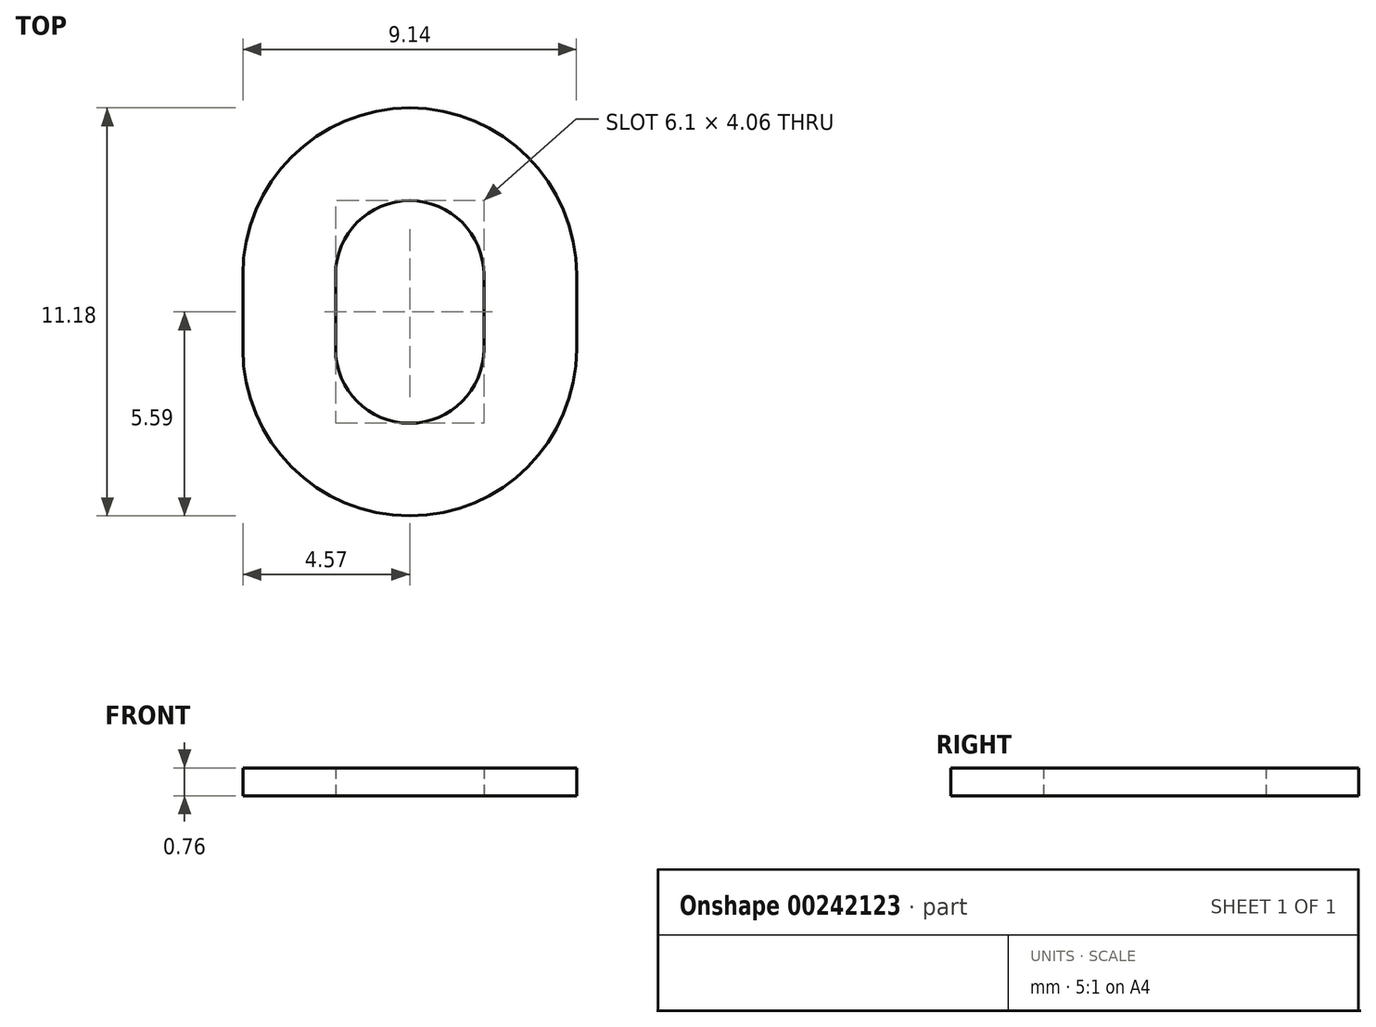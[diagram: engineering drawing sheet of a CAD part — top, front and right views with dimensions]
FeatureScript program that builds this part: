
annotation { "Feature Type Name" : "Feature", "Feature Type Description" : "" }
export const myFeature = defineFeature(function(context is Context, id is Id, definition is map)
    precondition{}
    {
        {
            var Q0;
            Q0=qCreatedBy(makeId("Top.planeOp"),FACE);
            var sketch = newSketch(context, id + "F0", { "sketchPlane" : qUnion([Q0])});
            skLineSegment(sketch, "E0", {"start": v(-2.03, 1.02) * mm, "end": v(-2.03, -1.02) * mm});
            skLineSegment(sketch, "E1", {"start": v(2.03, 1.02) * mm, "end": v(2.03, -1.02) * mm});
            skArc(sketch, "E2", {"start": v(2.03, 1.02) * mm, "mid": v(0, 3.05) * mm, "end": v(-2.03, 1.02) * mm});
            skArc(sketch, "E3", {"start": v(-2.03, -1.02) * mm, "mid": v(0, -3.05) * mm, "end": v(2.03, -1.02) * mm});
            skArc(sketch, "E4.0", {"start": v(4.57, 1.02) * mm, "mid": v(0, 5.59) * mm, "end": v(-4.57, 1.02) * mm});
            skLineSegment(sketch, "E4.1", {"start": v(4.57, 1.02) * mm, "end": v(4.57, -1.02) * mm});
            skArc(sketch, "E4.2", {"start": v(-4.57, -1.02) * mm, "mid": v(0, -5.59) * mm, "end": v(4.57, -1.02) * mm});
            skLineSegment(sketch, "E4.3", {"start": v(-4.57, 1.02) * mm, "end": v(-4.57, -1.02) * mm});
            skSolve(sketch);
        }
        {
            var Q0;
            Q0 = qSketchRegion(id + "F0", true);
            extrude(context, id + "F1", {"entities" : qUnion([Q0]), "depth" : 0.76 * mm});
        }
    });
